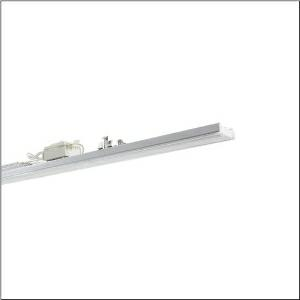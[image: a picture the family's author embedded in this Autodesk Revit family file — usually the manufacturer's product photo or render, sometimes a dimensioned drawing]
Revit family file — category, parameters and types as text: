
# Revit family: licross_21_recessed_mo_52tl12dn4axg3s
name_source: partatom
category: Lighting Fixtures
units: mm (PartAtom-declared; Revit-internal decimal feet)

## family parameters
Cut with Voids When Loaded = No
Host = Face
Light Source = No
Part Type = Normal
Room Calculation Point = No
Round Connector Dimension = Use Diameter
Shared = No

## types (1)
- --- (1 x LED, 950 lm, 6.7 W, 4000K)
    Apparent Load = 7 VA
    CIE Flux Codes = 72 92 99 100 100
    Color Rendering = 80
    Color Temperature = 4000K
    Default Elevation = 1800 mm
    Description = Licross 21 Recessed MO, luminaire insert, of sheet steel, galvanised, coil coated, white, length: 1.500mm, width: 66mm, height: 67mm, LED rated luminous flux: 10.280lm, light colour: 840, SDCM (Standard Deviation of Colour Matching)MacAdam ≤ 3 SDCM (initial), control gear: DALI 2 (for two DALI lines), with plug, 6-pole, with phase selection, for trunking rail, 14-core, mains connection: 220..240V, AC, 50/60Hz, rated input power: 62W, internal wiring halogen-free, for emergency light function, for trunking rail, 14-core, converter,control gear: single battery element, battery: LiFePO4, 9Ah, primary optical cover: cover, of PMMA, light emission: direct distribution, primary light characteristic: symmetric, protection rating (complete): IP40, insulation class (complete): insulation class I (protective earthing), certification: CE, UKCA, protection symbol: D if used in an environment without relevant dust loads with corresponding accessories, impact resistance: IK06, permissible ambient temperature for indoor applications: +5..+35°C, standard: EN 60598-2-22, LABS conformity tested according to VDMA 24364:2018-05, reducing of maximum allowable ambient temperature of 5°C with ceiling mounting, corresponds to IFS (International Featured Standards) requirements for safety and quality in the food industry, The light source and the operating device comply with the requirements of the Ecodesign Regulation (EU) 2019/2020 and are replaceable in accordance with this regulation, packaging unit: 1 piece
    Height = 58 mm
    Lamp = 1 x LED
    Lamp Light Flux = 950 lm
    Lamp Power = 6.7 W
    Lamp count = 1
    Length = 1500 mm
    Luminous efficacy = 142 lm/W
    Manufacturer = Siteco
    ModVariant = No
    Model = 52TL12DN4AXG3S
    Mounting Place = Ceiling
    Mounting Type = Pendant
    Number of Poles = 1
    OnlyDefault = Yes
    Power Factor = 1
    Product Name = Licross 21 Recessed MO
    Product group = luminaire insert | ceiling pendant
    ProductGroupID = 901
    Protection Class = Protection class I
    Protection Degree = IP 40
    RLX_Detail_Level = 1
    RLX_Emergency_Light_Flux = 0 lm
    RLX_Emergency_Type = 0
    RLX_Emergency_Type_DB = No
    RlxData = <blob elided: 25361 chars, md5=f4476b68>
    Socket = socket
    Standby Power = 0 W
    System Light Flux = 950 lm
    System Power = 7 W
    Type Comments = : emergency light operation: 3 h
    Type Image = l_1296930.jpg
    URL = http://relux.com
    VarID = @adj_110007
    Voltage = 0 V
    Weight = 0.00 kg
    Width = 66 mm

## geometry (parser evidence)
native form markers: Blend x4, Sweep x11
no freeform markers — native parametric forms only
